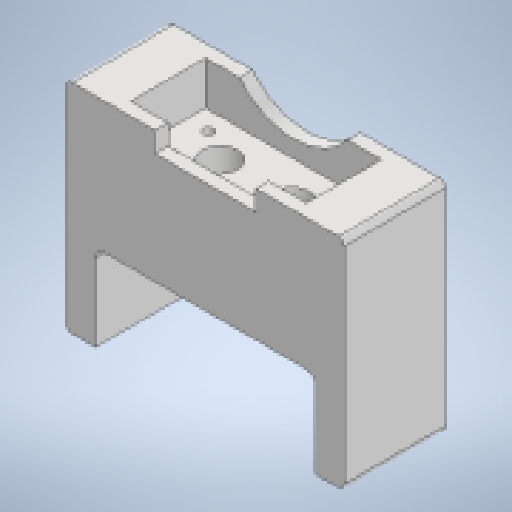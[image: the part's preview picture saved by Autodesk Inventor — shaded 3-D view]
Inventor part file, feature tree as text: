
AUTODESK INVENTOR PART (.ipt)
format: ipt  version: 2023 (Build 270158000, 158)  size: 220,672 bytes
history: native  units: in
note: dims shown in document units (in); Inventor stores cm internally (conversion verified against a paired STEP export)
features: extrude x8, sketch x7, fillet x2
ambient origin geometry x8: Origin, YZ Plane, XZ Plane, XY Plane, X Axis, Y Axis, Z Axis, Center Point
bodies: Solid1 (feature_tree)
feature tree (17):
  sketch  "Sketch1"  dims[d0=0.9843in d1=2.3622in]
  extrude  "Extrusion1"  Depth=0.9843in
  extrude  "Extrusion2"  Depth=0.0197in
  extrude  "Extrusion3"  Depth=0.0197in
  extrude  "Extrusion4"  Depth=1.811in
  extrude  "Extrusion5"  Depth=3.7874in
  extrude  "Extrusion6"  Depth=0.3937in TaperAngle=0.0deg
  fillet  "Fillet1"  Radius=1.3937in
  fillet  "Fillet2"  Radius=0.3937in
  extrude  "Extrusion7"  Depth=3.0in
  extrude  "Extrusion8"  Depth=0.125in
  sketch  "Sketch2"  dims[d2=0.0197in d3=0.0197in]
  sketch  "Sketch3"  dims[d4=0.0197in d5=0.0197in]
  sketch  "Sketch4"  dims[d6=0.1417in d7=1.811in]
  sketch  "Sketch5"  dims[d8=0.5118in d9=3.7874in]
  sketch  "Sketch6"  dims[d10=1.378in d11=0.3937in d12=0.0in d13=1.3937in d14=0.0in]
  sketch  "Sketch7"  dims[d15=0.3937in d16=0.1969in d17=0.0in d18=0.0in d19=0.3937in d20=1.1969in d21=0.0in d22=0.0in d23=3.0in d24=0.125in d25=0.3937in d26=1.1811in d27=0.3937in d28=0.0in d29=0.2362in d30=0.9843in d31=0.3937in d32=0.0in d34=0.4724in d35=0.3937in d36=0.0in d37=0.0787in d38=0.0787in d39=1.5118in d40=1.378in d41=2.0812in d42=0.0in d44=0.9843in d45=0.3937in d46=0.3937in d47=0.0in]
